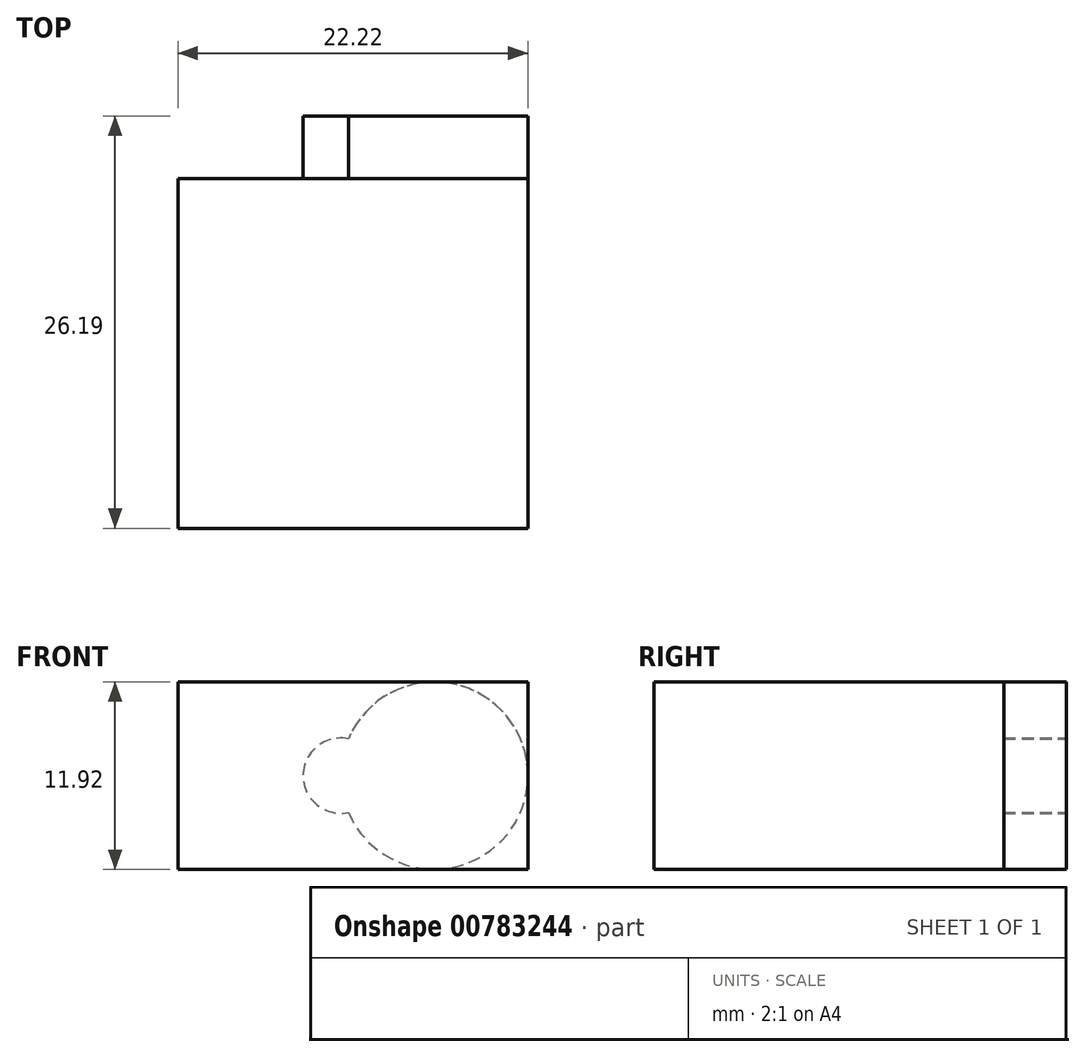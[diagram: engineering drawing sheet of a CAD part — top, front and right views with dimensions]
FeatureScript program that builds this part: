
annotation { "Feature Type Name" : "Feature", "Feature Type Description" : "" }
export const myFeature = defineFeature(function(context is Context, id is Id, definition is map)
    precondition{}
    {
        {
            var Q0;
            Q0=qCreatedBy(makeId("Front.planeOp"),FACE);
            var sketch = newSketch(context, id + "F0", { "sketchPlane" : qUnion([Q0])});
            skLineSegment(sketch, "E0.bottom", {"start": v(-41.33, 28.9) * mm, "end": v(-19.1, 28.9) * mm});
            skLineSegment(sketch, "E0.top", {"start": v(-41.33, 17) * mm, "end": v(-19.1, 17) * mm});
            skLineSegment(sketch, "E0.left", {"start": v(-41.33, 28.9) * mm, "end": v(-41.33, 17) * mm});
            skLineSegment(sketch, "E0.right", {"start": v(-19.1, 28.9) * mm, "end": v(-19.1, 17) * mm});
            skArc(sketch, "E1", {"start": v(-30.51, 20.61) * mm, "mid": v(-19.1, 22.95) * mm, "end": v(-30.51, 25.29) * mm});
            skArc(sketch, "E2", {"start": v(-30.51, 25.29) * mm, "mid": v(-33.38, 22.95) * mm, "end": v(-30.51, 20.61) * mm});
            skSolve(sketch);
        }
        {
            var Q0;
            {var subQ1=sQuery(id+"F0.wireOp",EDGE,"E0.bottom");Q0=makeQuery(id+"F0.imprint","IMPRINT",FACE,{"disambiguationData":[TD([[makeQuery(id+"F0.imprint","IMPRINT",EDGE,{"derivedFrom":subQ1}),-1.0]])]});}
            var Q1;
            {var subQ0=sQuery(id+"F0.wireOp",EDGE,"E2");Q1=makeQuery(id+"F0.imprint","IMPRINT",FACE,{"disambiguationData":[TD([[makeQuery(id+"F0.imprint","IMPRINT",EDGE,{"derivedFrom":subQ0}),1.0]])]});}
            extrude(context, id + "F1", {"entities" : qUnion([Q0, Q1]), "depth" : 26.2 * mm, "offsetDistance" : 25.4 * mm, "hasSecondDirection" : true, "secondDirectionOppositeDirection" : true, "secondDirectionDepth" : -3.96 * mm});
        }
        {
            var Q0;
            {var subQ0=sQuery(id+"F0.wireOp",EDGE,"E2");Q0=makeQuery(id+"F0.imprint","IMPRINT",FACE,{"disambiguationData":[TD([[makeQuery(id+"F0.imprint","IMPRINT",EDGE,{"derivedFrom":subQ0}),1.0]])]});}
            extrude(context, id + "F2", {"entities" : qUnion([Q0]), "operationType" : NewBodyOperationType.ADD, "depth" : 25.4 * mm, "offsetDistance" : 25.4 * mm});
        }
    });
